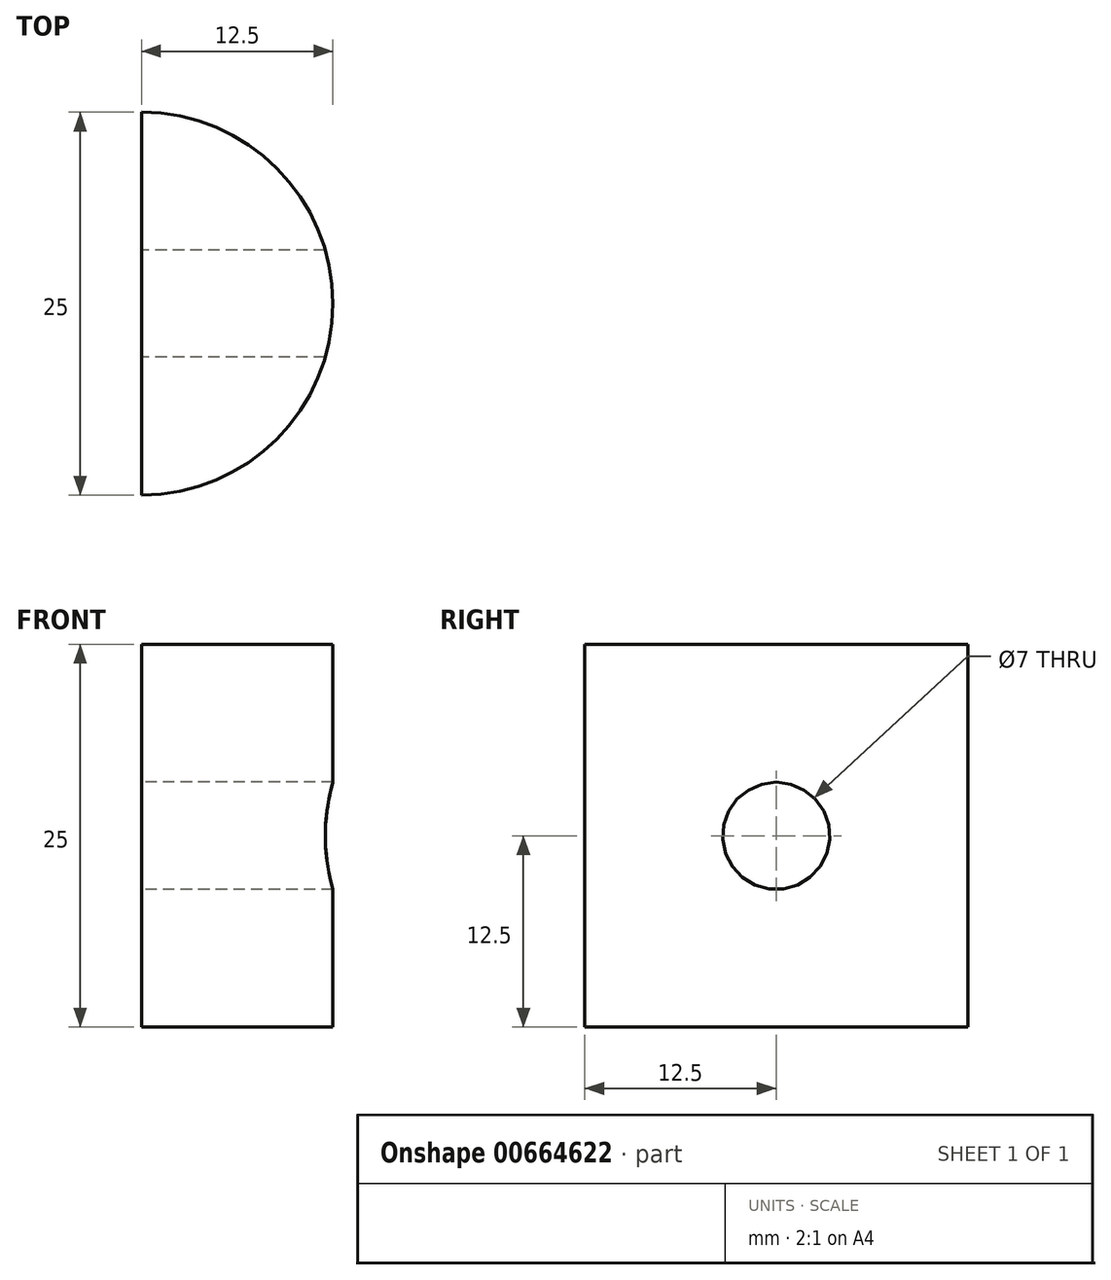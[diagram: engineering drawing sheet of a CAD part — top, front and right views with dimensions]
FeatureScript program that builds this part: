
annotation { "Feature Type Name" : "Feature", "Feature Type Description" : "" }
export const myFeature = defineFeature(function(context is Context, id is Id, definition is map)
    precondition{}
    {
        {
            var Q0;
            Q0=qCreatedBy(makeId("Top.planeOp"),FACE);
            var sketch = newSketch(context, id + "F0", { "sketchPlane" : qUnion([Q0])});
            skArc(sketch, "E0", {"start": v(0, -12.5) * mm, "mid": v(12.5, 0) * mm, "end": v(0, 12.5) * mm});
            skLineSegment(sketch, "E1", {"start": v(0, 21.15) * mm, "end": v(0, -27.38) * mm, "construction": true});
            skLineSegment(sketch, "E2", {"start": v(0, 12.5) * mm, "end": v(0, -12.5) * mm});
            skSolve(sketch);
        }
        {
            var Q0;
            Q0 = qSketchRegion(id + "F0", true);
            extrude(context, id + "F1", {"entities" : qUnion([Q0]), "depth" : 25 * mm, "offsetDistance" : 25 * mm});
        }
        {
            var Q0;
            Q0=makeQuery(id+"F1.opExtrude","SWEPT_FACE",FACE,{"disambiguationData":[OSD([sQuery(id+"F0.wireOp",EDGE,"E2")])]});
            var sketch = newSketch(context, id + "F2", { "sketchPlane" : qUnion([Q0])});
            skLineSegment(sketch, "E3", {"start": v(12.5, 25) * mm, "end": v(12.5, 0) * mm});
            skCircle(sketch, "E4", {"center": v(0, 12.5) * mm, "radius": 3.5 * mm});
            skPoint(sketch, "E5.orphan", {"position": v(-12.5, 25) * mm});
            skSolve(sketch);
        }
        {
            var Q0;
            Q0=makeQuery(id+"F2.imprint","IMPRINT",FACE,{"disambiguationData":[TD([[makeQuery(id+"F2.imprint","IMPRINT",EDGE,{"derivedFrom":sQuery(id+"F2.wireOp",EDGE,"E4")}),1.0]])]});
            extrude(context, id + "F3", {"entities" : qUnion([Q0]), "operationType" : NewBodyOperationType.REMOVE, "oppositeDirection" : true, "depth" : 25 * mm, "offsetDistance" : 25 * mm});
        }
    });
